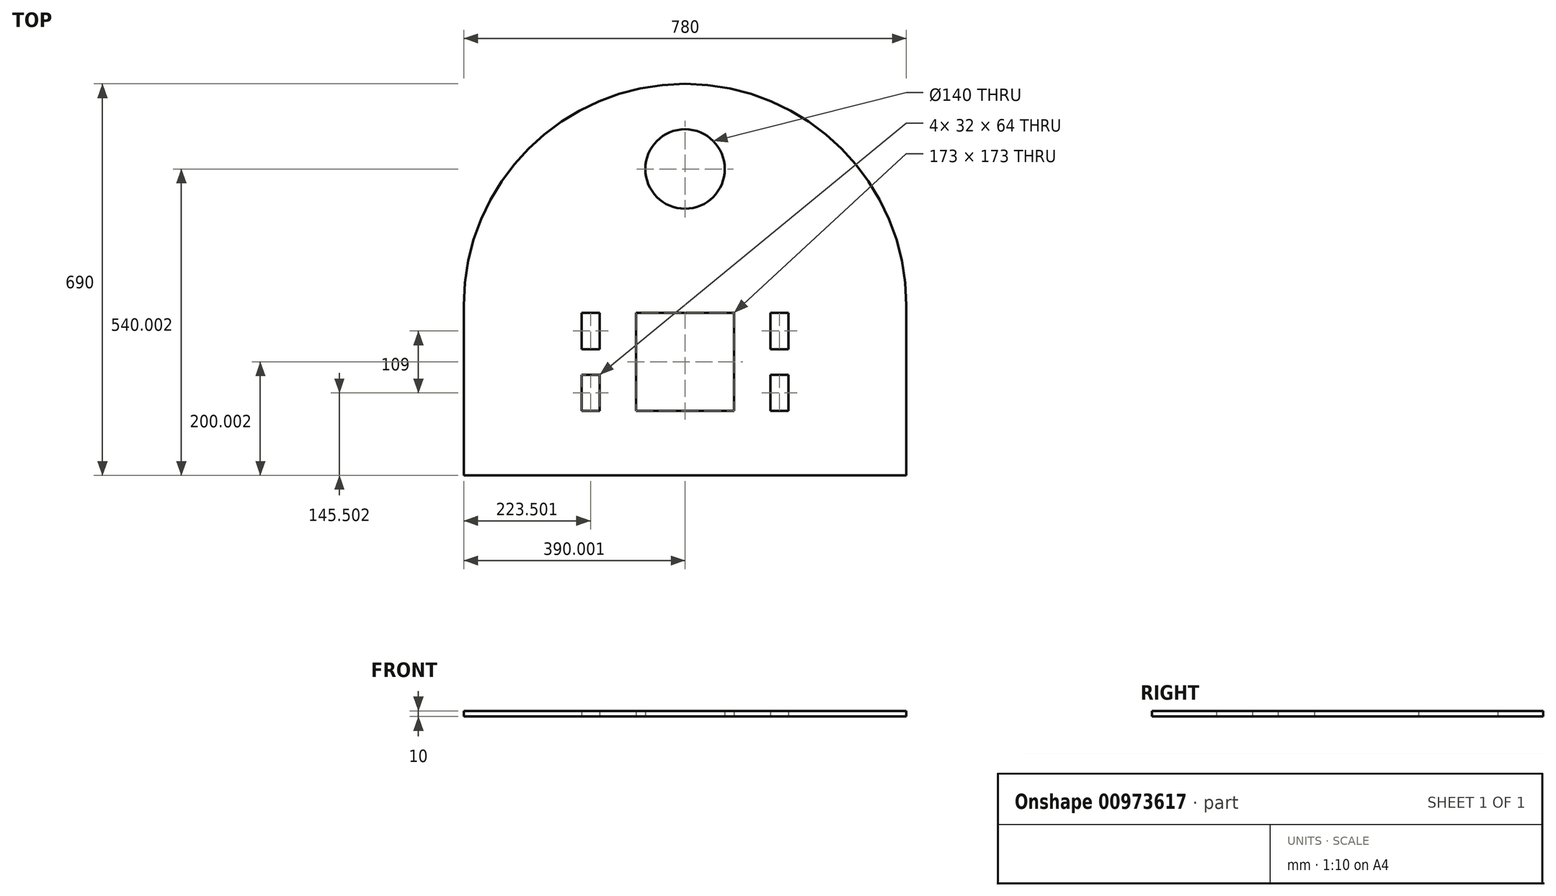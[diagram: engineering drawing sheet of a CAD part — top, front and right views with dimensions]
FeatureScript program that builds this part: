
annotation { "Feature Type Name" : "Feature", "Feature Type Description" : "" }
export const myFeature = defineFeature(function(context is Context, id is Id, definition is map)
    precondition{}
    {
        {
            var Q0;
            Q0=qCreatedBy(makeId("Top.planeOp"),FACE);
            var sketch = newSketch(context, id + "F0", { "sketchPlane" : qUnion([Q0])});
            skLineSegment(sketch, "E0.rect.bottom", {"start": v(86.44, 86.5) * mm, "end": v(-86.56, 86.5) * mm});
            skLineSegment(sketch, "E0.rect.top", {"start": v(86.44, -86.5) * mm, "end": v(-86.56, -86.5) * mm});
            skLineSegment(sketch, "E0.rect.left", {"start": v(86.44, 86.5) * mm, "end": v(86.44, -86.5) * mm});
            skLineSegment(sketch, "E0.rect.right", {"start": v(-86.56, 86.5) * mm, "end": v(-86.56, -86.5) * mm});
            skPoint(sketch, "E0.rect.middle", {"position": v(-0.06, 0) * mm});
            skLineSegment(sketch, "E1", {"start": v(-390.06, -200) * mm, "end": v(389.94, -200) * mm});
            skPoint(sketch, "E2", {"position": v(-0.06, 86.5) * mm});
            skLineSegment(sketch, "E3", {"start": v(-390.06, -200) * mm, "end": v(-390.06, 100) * mm});
            skLineSegment(sketch, "E4.MirrorCS", {"start": v(389.94, -200) * mm, "end": v(389.94, 100) * mm});
            skArc(sketch, "E5", {"start": v(-390.06, 100) * mm, "mid": v(-0.06, 490) * mm, "end": v(389.94, 100) * mm});
            skCircle(sketch, "E6", {"center": v(-0.06, 340) * mm, "radius": 70 * mm});
            skLineSegment(sketch, "E7.bottom", {"start": v(-182.56, 86.5) * mm, "end": v(-150.56, 86.5) * mm});
            skLineSegment(sketch, "E7.top", {"start": v(-182.56, 22.5) * mm, "end": v(-150.56, 22.5) * mm});
            skLineSegment(sketch, "E7.left", {"start": v(-182.56, 86.5) * mm, "end": v(-182.56, 22.5) * mm});
            skLineSegment(sketch, "E7.right", {"start": v(-150.56, 86.5) * mm, "end": v(-150.56, 22.5) * mm});
            skLineSegment(sketch, "E8.bottom", {"start": v(-182.56, -22.5) * mm, "end": v(-150.56, -22.5) * mm});
            skLineSegment(sketch, "E8.right", {"start": v(-150.56, -22.5) * mm, "end": v(-150.56, -86.5) * mm});
            skLineSegment(sketch, "E8.top", {"start": v(-182.56, -86.5) * mm, "end": v(-150.56, -86.5) * mm});
            skLineSegment(sketch, "E8.left", {"start": v(-182.56, -22.5) * mm, "end": v(-182.56, -86.5) * mm});
            skLineSegment(sketch, "E9.MirrorCS", {"start": v(182.44, -22.5) * mm, "end": v(182.44, -86.5) * mm});
            skLineSegment(sketch, "E10.MirrorCS", {"start": v(182.44, -86.5) * mm, "end": v(150.44, -86.5) * mm});
            skLineSegment(sketch, "E11.MirrorCS", {"start": v(150.44, -22.5) * mm, "end": v(150.44, -86.5) * mm});
            skLineSegment(sketch, "E12.MirrorCS", {"start": v(182.44, -22.5) * mm, "end": v(150.44, -22.5) * mm});
            skLineSegment(sketch, "E13.MirrorCS", {"start": v(182.44, 86.5) * mm, "end": v(182.44, 22.5) * mm});
            skLineSegment(sketch, "E14.MirrorCS", {"start": v(182.44, 22.5) * mm, "end": v(150.44, 22.5) * mm});
            skLineSegment(sketch, "E15.MirrorCS", {"start": v(150.44, 86.5) * mm, "end": v(150.44, 22.5) * mm});
            skLineSegment(sketch, "E16.MirrorCS", {"start": v(182.44, 86.5) * mm, "end": v(150.44, 86.5) * mm});
            skSolve(sketch);
        }
        {
            var Q0;
            Q0 = qSketchRegion(id + "F0", true);
            extrude(context, id + "F1", {"entities" : qUnion([Q0]), "depth" : 10 * mm, "offsetDistance" : 25 * mm});
        }
    });
